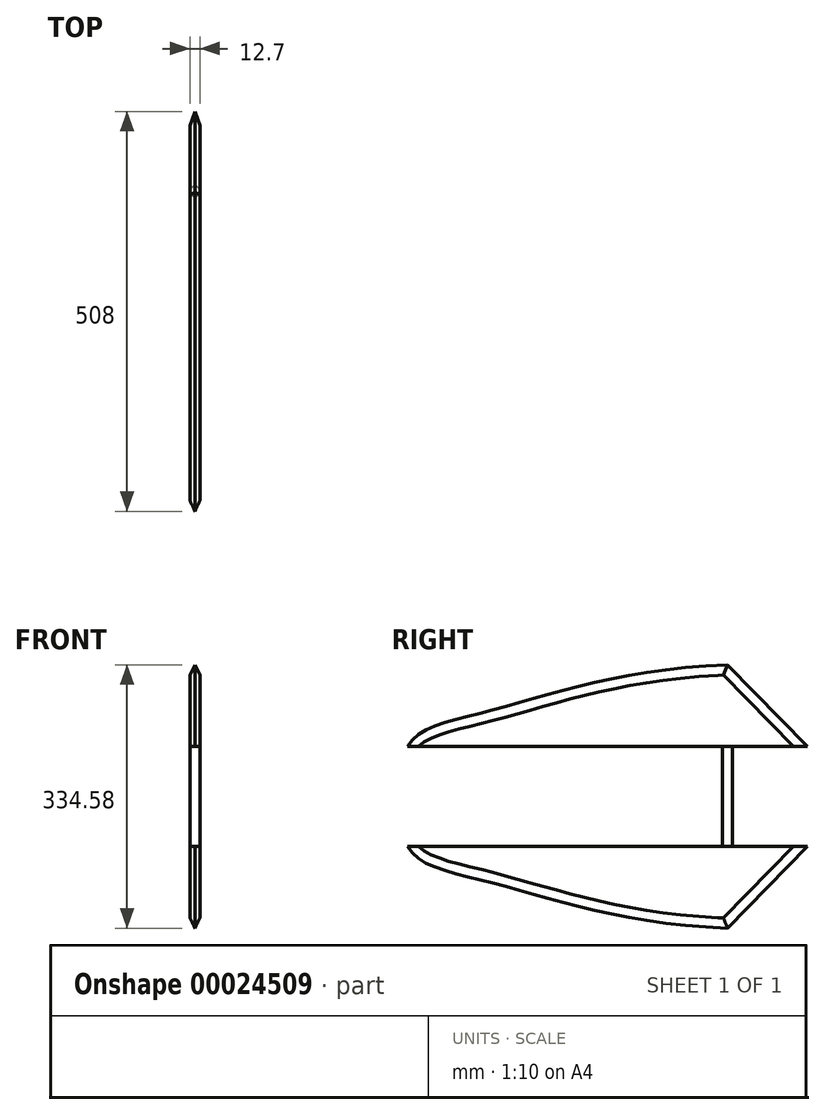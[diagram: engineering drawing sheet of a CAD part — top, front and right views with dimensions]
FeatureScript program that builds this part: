
annotation { "Feature Type Name" : "Feature", "Feature Type Description" : "" }
export const myFeature = defineFeature(function(context is Context, id is Id, definition is map)
    precondition{}
    {
        {
            var Q0;
            Q0=qCreatedBy(makeId("Right.planeOp"),FACE);
            var sketch = newSketch(context, id + "F0", { "sketchPlane" : qUnion([Q0])});
            skLineSegment(sketch, "E0", {"start": v(0, 0) * mm, "end": v(0, 63.5) * mm});
            skLineSegment(sketch, "E1", {"start": v(0, 63.5) * mm, "end": v(-406.4, 63.5) * mm});
            skLineSegment(sketch, "E2", {"start": v(0, 63.5) * mm, "end": v(101.6, 63.5) * mm});
            skFitSpline(sketch, "E3", {"points": [v(-406.4, 63.5) * mm, v(-304.62, 108.25) * mm, v(0, 167.3) * mm], "startDerivative": vector(112.7, 208.48) * mm, "endDerivative": vector(638.98, 20.9) * mm});
            skLineSegment(sketch, "E4", {"start": v(0, 167.3) * mm, "end": v(101.6, 63.5) * mm});
            skSolve(sketch);
        }
        {
            var Q0;
            Q0=makeQuery(id+"F0.imprint","IMPRINT",FACE,{"disambiguationData":[TD([[makeQuery(id+"F0.imprint","IMPRINT",EDGE,{"derivedFrom":sQuery(id+"F0.wireOp",EDGE,"E1")}),-1.0]])]});
            extrude(context, id + "F1", {"entities" : qUnion([Q0]), "depth" : 12.7 * mm});
        }
        {
            var Q0;
            Q0=makeQuery(id+"F1.opExtrude","SWEPT_FACE",FACE,{"disambiguationData":[OSD([sQuery(id+"F0.wireOp",EDGE,"E1"),sQuery(id+"F0.wireOp",EDGE,"E2")])]});
            var sketch = newSketch(context, id + "F2", { "sketchPlane" : qUnion([Q0])});
            skCircle(sketch, "E5", {"center": v(6.35, 0) * mm, "radius": 6.35 * mm});
            skSolve(sketch);
        }
        {
            var Q0;
            Q0 = qSketchRegion(id + "F2", true);
            extrude(context, id + "F3", {"entities" : qUnion([Q0]), "operationType" : NewBodyOperationType.ADD, "depth" : 63.5 * mm});
        }
        {
            var Q0;
            {var subQ0=sQuery(id+"F0.wireOp",EDGE,"E1");var subQ1=sQuery(id+"F0.wireOp",EDGE,"E2");var subQ2=makeQuery(id+"F1.opExtrude","SWEPT_FACE",FACE,{"disambiguationData":[OSD([subQ0,subQ1])]});var subQ3=sQuery(id+"F0.wireOp",EDGE,"E4");Q0=makeQuery(id+"F3.boolean.opBoolean","SPLIT",FACE,{"disambiguationData":[TD([makeQuery(id+"F1.opExtrude","SWEPT_FACE",FACE,{"disambiguationData":[OSD([subQ3])]})])],"derivedFrom":subQ2});}
            var sketch = newSketch(context, id + "F4", { "sketchPlane" : qUnion([Q0])});
            skLineSegment(sketch, "E6", {"start": v(6.35, -101.6) * mm, "end": v(12.7, -83.43) * mm});
            skLineSegment(sketch, "E7", {"start": v(0, -83.43) * mm, "end": v(6.35, -101.6) * mm});
            skSolve(sketch);
        }
        {
            var Q0;
            {var subQ4=sQuery(id+"F4.wireOp",EDGE,"E6");Q0=makeQuery(id+"F4.imprint","IMPRINT",FACE,{"disambiguationData":[TD([[makeQuery(id+"F4.imprint","IMPRINT",EDGE,{"derivedFrom":subQ4}),-1.0]])]});}
            var Q1;
            {var subQ4=sQuery(id+"F4.wireOp",EDGE,"E7");Q1=makeQuery(id+"F4.imprint","IMPRINT",FACE,{"disambiguationData":[TD([[makeQuery(id+"F4.imprint","IMPRINT",EDGE,{"derivedFrom":subQ4}),-1.0]])]});}
            var Q2;
            Q2=makeQuery(id+"F1.opExtrude","CAP_EDGE",EDGE,{"disambiguationData":[OSD([sQuery(id+"F0.wireOp",EDGE,"E4")])],"isStart":true});
            var Q3;
            Q3=makeQuery(id+"F1.opExtrude","CAP_EDGE",EDGE,{"disambiguationData":[OSD([sQuery(id+"F0.wireOp",EDGE,"E3")])],"isStart":true});
            sweep(context, id + "F5", {"operationType" : NewBodyOperationType.REMOVE, "profiles" : qUnion([Q0, Q1]), "path" : qUnion([Q2, Q3])});
        }
        {
            var Q0;
            Q0=makeQuery(id+"F1.opExtrude","SWEPT_BODY",BODY,{"disambiguationData":[OSD([sQuery(id+"F0.wireOp",EDGE,"E1"),sQuery(id+"F0.wireOp",EDGE,"E2"),sQuery(id+"F0.wireOp",EDGE,"E3"),sQuery(id+"F0.wireOp",EDGE,"E4")])]});
            var Q1;
            Q1=makeQuery(id+"F3.opExtrude","CAP_FACE",FACE,{"disambiguationData":[OSD([sQuery(id+"F2.wireOp",EDGE,"E5")])],"isStart":false});
            mirror(context, id + "F6", {"operationType" : NewBodyOperationType.ADD, "entities" : qUnion([Q0]), "mirrorPlane" : qUnion([Q1])});
        }
    });
